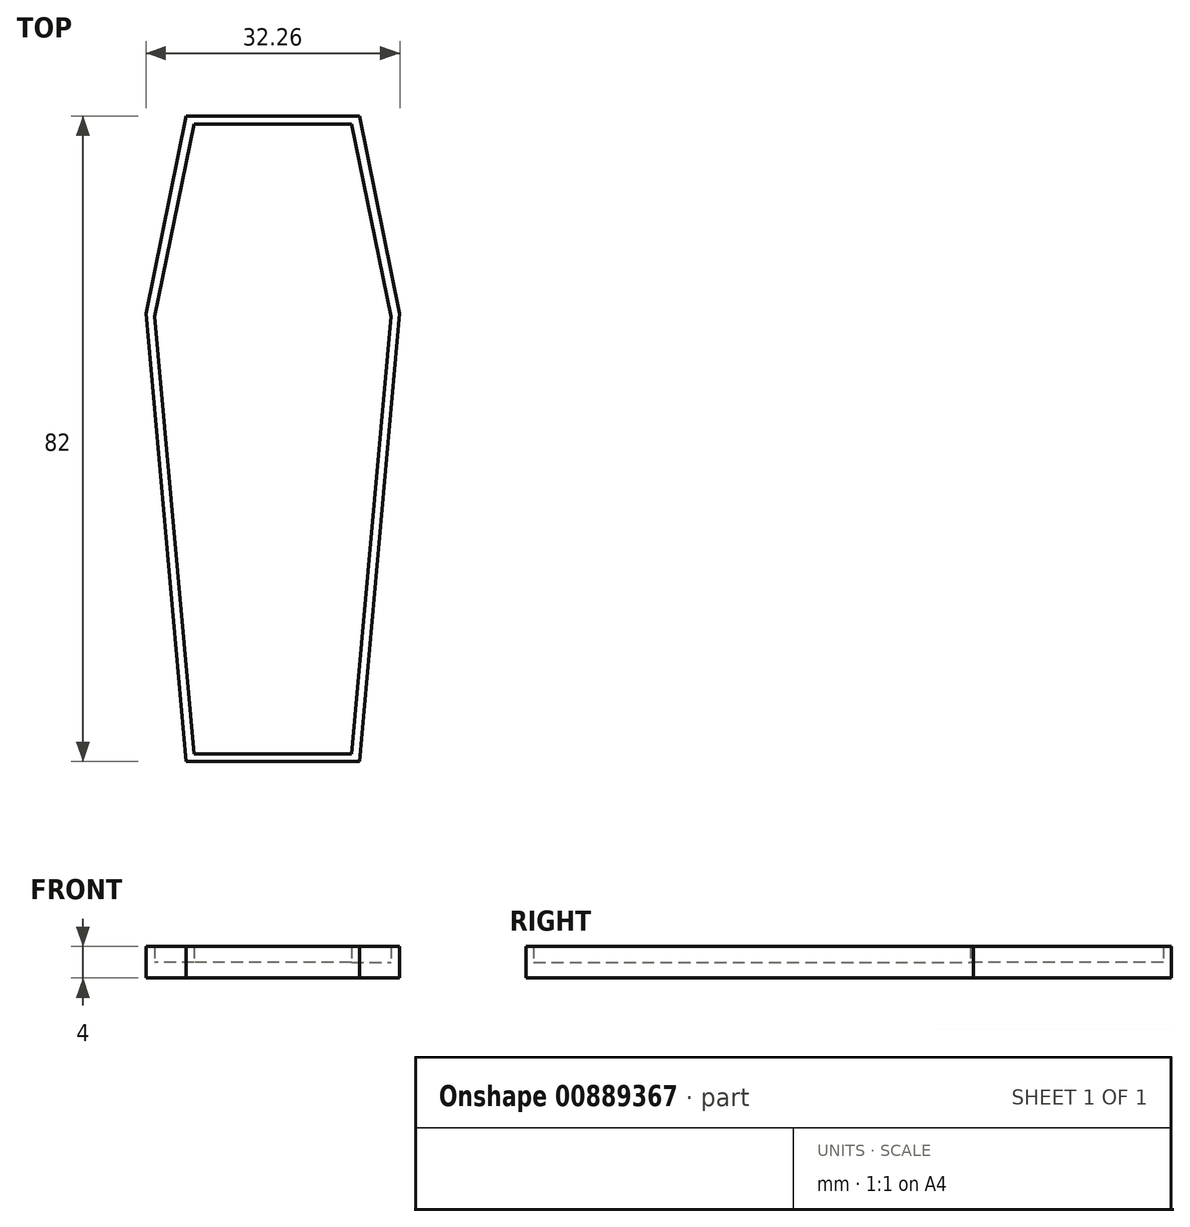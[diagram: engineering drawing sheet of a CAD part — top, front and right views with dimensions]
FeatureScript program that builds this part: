
annotation { "Feature Type Name" : "Feature", "Feature Type Description" : "" }
export const myFeature = defineFeature(function(context is Context, id is Id, definition is map)
    precondition{}
    {
        {
            var Q0;
            Q0=qCreatedBy(makeId("Top.planeOp"),FACE);
            var sketch = newSketch(context, id + "F0", { "sketchPlane" : qUnion([Q0])});
            skLineSegment(sketch, "E0.bottom", {"start": v(10, 40) * mm, "end": v(-10, 40) * mm});
            skLineSegment(sketch, "E0.top", {"start": v(10, -40) * mm, "end": v(-10, -40) * mm});
            skLineSegment(sketch, "E0.left", {"start": v(10, 40) * mm, "end": v(10, -40) * mm});
            skLineSegment(sketch, "E0.right", {"start": v(-10, 40) * mm, "end": v(-10, -40) * mm});
            skPoint(sketch, "E0.middle", {"position": v(0, 0) * mm});
            skLineSegment(sketch, "E1", {"start": v(-10, 40) * mm, "end": v(-15, 15.5) * mm});
            skLineSegment(sketch, "E2", {"start": v(-10, -40) * mm, "end": v(-15, 15.5) * mm});
            skLineSegment(sketch, "E3.MirrorCS", {"start": v(10, -40) * mm, "end": v(15, 15.5) * mm});
            skLineSegment(sketch, "E4.MirrorCS", {"start": v(10, 40) * mm, "end": v(15, 15.5) * mm});
            skLineSegment(sketch, "E5.bottom", {"start": v(-11, 41) * mm, "end": v(11, 41) * mm});
            skLineSegment(sketch, "E5.top", {"start": v(-11, -41) * mm, "end": v(11, -41) * mm});
            skLineSegment(sketch, "E5.left", {"start": v(-11, 41) * mm, "end": v(-11, -41) * mm});
            skLineSegment(sketch, "E5.right", {"start": v(11, 41) * mm, "end": v(11, -41) * mm});
            skLineSegment(sketch, "E6", {"start": v(-11, 41) * mm, "end": v(-16.13, 15.9) * mm});
            skLineSegment(sketch, "E7", {"start": v(-16.13, 15.9) * mm, "end": v(-11, -41) * mm});
            skLineSegment(sketch, "E8.MirrorCS", {"start": v(11, 41) * mm, "end": v(16.13, 15.9) * mm});
            skLineSegment(sketch, "E9.MirrorCS", {"start": v(16.13, 15.9) * mm, "end": v(11, -41) * mm});
            skSolve(sketch);
        }
        {
            var Q0;
            {var subQ0=sQuery(id+"F0.wireOp",EDGE,"E2");var subQ1=sQuery(id+"F0.wireOp",EDGE,"E1");var subQ2=makeQuery(id+"F0.imprint","INTERSECT",VERTEX,{"derivedFrom":[subQ1,subQ0]});Q0=makeQuery(id+"F0.imprint","IMPRINT",FACE,{"disambiguationData":[TD([[makeQuery(id+"F0.imprint","IMPRINT",EDGE,{"disambiguationData":[TD([[subQ2,1.0]])],"derivedFrom":subQ1}),1.0]])]});}
            var Q1;
            Q1=makeQuery(id+"F0.imprint","IMPRINT",FACE,{"disambiguationData":[TD([[makeQuery(id+"F0.imprint","IMPRINT",EDGE,{"derivedFrom":sQuery(id+"F0.wireOp",EDGE,"E0.bottom")}),1.0]])]});
            var Q2;
            {var subQ0=sQuery(id+"F0.wireOp",EDGE,"E4.MirrorCS");var subQ1=sQuery(id+"F0.wireOp",EDGE,"E3.MirrorCS");var subQ2=makeQuery(id+"F0.imprint","INTERSECT",VERTEX,{"derivedFrom":[subQ1,subQ0]});Q2=makeQuery(id+"F0.imprint","IMPRINT",FACE,{"disambiguationData":[TD([[makeQuery(id+"F0.imprint","IMPRINT",EDGE,{"disambiguationData":[TD([[subQ2,1.0]])],"derivedFrom":subQ1}),1.0]])]});}
            var Q3;
            {var subQ0=sQuery(id+"F0.wireOp",EDGE,"E0.left");Q3=makeQuery(id+"F0.imprint","IMPRINT",FACE,{"disambiguationData":[TD([[makeQuery(id+"F0.imprint","IMPRINT",EDGE,{"derivedFrom":subQ0}),1.0]])]});}
            var Q4;
            {var subQ0=sQuery(id+"F0.wireOp",EDGE,"E0.right");Q4=makeQuery(id+"F0.imprint","IMPRINT",FACE,{"disambiguationData":[TD([[makeQuery(id+"F0.imprint","IMPRINT",EDGE,{"derivedFrom":subQ0}),-1.0]])]});}
            extrude(context, id + "F1", {"entities" : qUnion([Q0, Q1, Q2, Q3, Q4]), "depth" : 2 * mm, "offsetDistance" : 25 * mm});
        }
        {
            var Q0;
            {var subQ7=sQuery(id+"F0.wireOp",EDGE,"E6");Q0=makeQuery(id+"F0.imprint","IMPRINT",FACE,{"disambiguationData":[TD([[makeQuery(id+"F0.imprint","IMPRINT",EDGE,{"derivedFrom":subQ7}),1.0]])]});}
            var Q1;
            {var subQ2=sQuery(id+"F0.wireOp",EDGE,"E0.bottom");Q1=makeQuery(id+"F0.imprint","IMPRINT",FACE,{"disambiguationData":[TD([[makeQuery(id+"F0.imprint","IMPRINT",EDGE,{"derivedFrom":subQ2}),-1.0]])]});}
            var Q2;
            {var subQ0=sQuery(id+"F0.wireOp",EDGE,"E8.MirrorCS");Q2=makeQuery(id+"F0.imprint","IMPRINT",FACE,{"disambiguationData":[TD([[makeQuery(id+"F0.imprint","IMPRINT",EDGE,{"derivedFrom":subQ0}),-1.0]])]});}
            var Q3;
            {var subQ2=sQuery(id+"F0.wireOp",EDGE,"E0.top");Q3=makeQuery(id+"F0.imprint","IMPRINT",FACE,{"disambiguationData":[TD([[makeQuery(id+"F0.imprint","IMPRINT",EDGE,{"derivedFrom":subQ2}),1.0]])]});}
            extrude(context, id + "F2", {"entities" : qUnion([Q0, Q1, Q2, Q3]), "operationType" : NewBodyOperationType.ADD, "depth" : 4 * mm, "offsetDistance" : 25 * mm});
        }
    });
